# Revit family: P1713_1_Hole_1_Slot_90_Fitting
name_source: partatom
category: Generic Models
units: mm (PartAtom-declared; Revit-internal decimal feet)

## family parameters
Always vertical = No
Can host rebar = No
Cut with Voids When Loaded = No
Part Type = Normal
Room Calculation Point = No
Round Connector Dimension = Use Diameter
Shared = No
Work Plane-Based = Yes

## types (3) — shared parameters
Cost = $0.00
Description = P1713 - 1 Hole, 1 Slot, 90° Fitting
Manufacturer = Atkore Unistrut
Model = P1713
Salsify ID1 = US-P1713
URL = https://www.atkore.com
zero-valued in all types: Default Elevation

## per-type parameters (varying)
| type | Material | UPC | Weight |
| P1713 EG | Electro Galvanized | "786364022017" | 0.97 lb |
| P1713 GR | Green | "786364022024" | 0.97 lb |
| P1713 HG | Hot Dip Galvanized | "786364022031" | 1.03 lb |

note: column(s) folded — value = type name in every type: Part Number

## geometry (parser evidence)
native form markers: Sweep x2
no freeform markers — native parametric forms only
